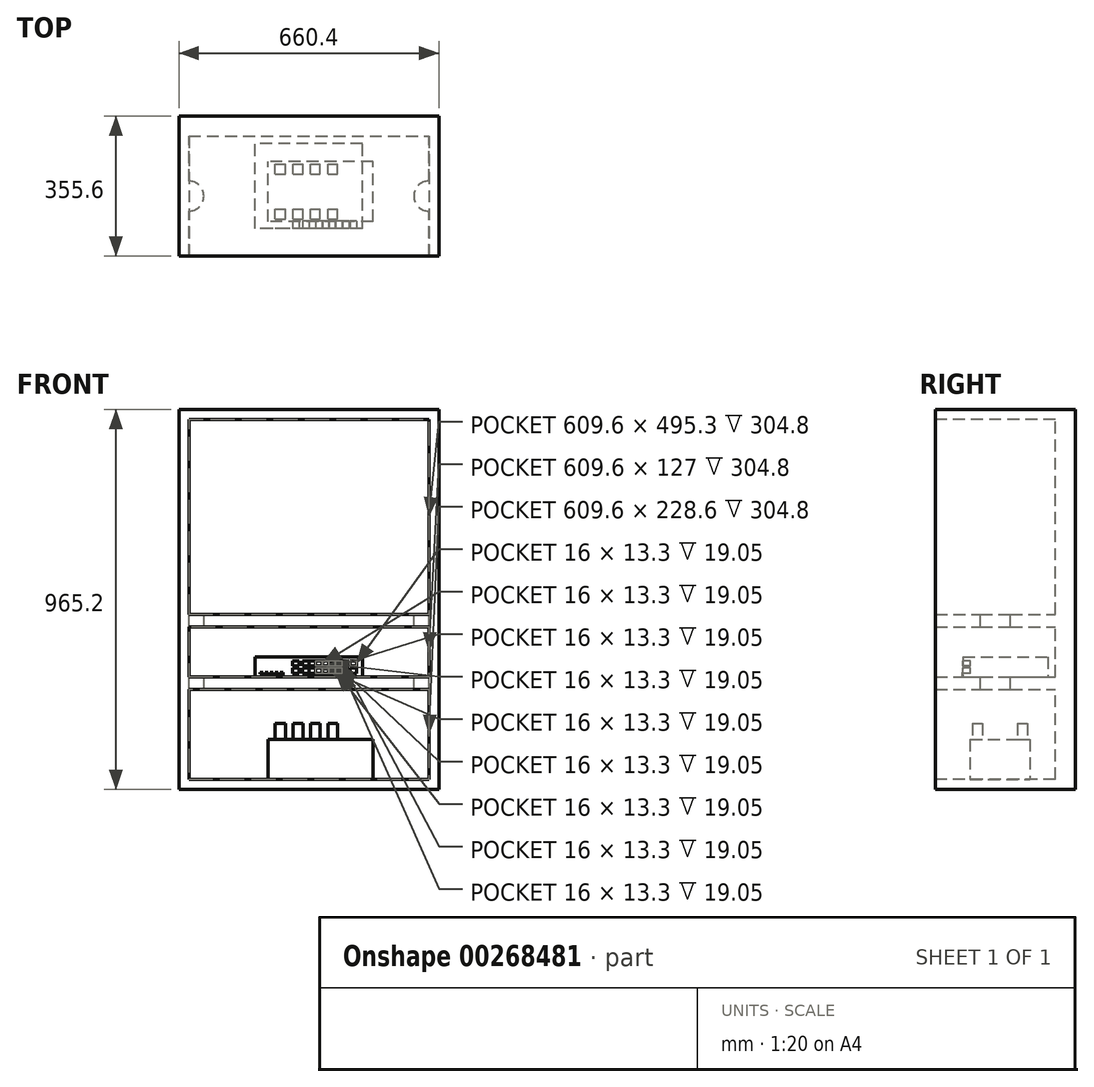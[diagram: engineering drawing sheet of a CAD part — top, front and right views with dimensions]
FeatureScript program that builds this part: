
annotation { "Feature Type Name" : "Feature", "Feature Type Description" : "" }
export const myFeature = defineFeature(function(context is Context, id is Id, definition is map)
    precondition{}
    {
        {
            var Q0;
            Q0=qCreatedBy(makeId("Top.planeOp"),FACE);
            var sketch = newSketch(context, id + "F0", { "sketchPlane" : qUnion([Q0])});
            skLineSegment(sketch, "E0.bottom", {"start": v(330.2, -177.8) * mm, "end": v(-330.2, -177.8) * mm});
            skLineSegment(sketch, "E0.top", {"start": v(330.2, 177.8) * mm, "end": v(-330.2, 177.8) * mm});
            skLineSegment(sketch, "E0.left", {"start": v(330.2, -177.8) * mm, "end": v(330.2, 177.8) * mm});
            skLineSegment(sketch, "E0.right", {"start": v(-330.2, -177.8) * mm, "end": v(-330.2, 177.8) * mm});
            skPoint(sketch, "E0.middle", {"position": v(0, 0) * mm});
            skSolve(sketch);
        }
        {
            var Q0;
            Q0 = qSketchRegion(id + "F0", true);
            extrude(context, id + "F1", {"entities" : qUnion([Q0]), "depth" : 965.2 * mm});
        }
        {
            var Q0;
            Q0=makeQuery(id+"F1.opExtrude","SWEPT_FACE",FACE,{"disambiguationData":[OSD([sQuery(id+"F0.wireOp",EDGE,"E0.bottom")])]});
            var sketch = newSketch(context, id + "F2", { "sketchPlane" : qUnion([Q0])});
            skLineSegment(sketch, "E1.bottom", {"start": v(304.8, 25.4) * mm, "end": v(-304.8, 25.4) * mm});
            skLineSegment(sketch, "E1.top", {"start": v(304.8, 939.8) * mm, "end": v(-304.8, 939.8) * mm});
            skLineSegment(sketch, "E1.left", {"start": v(304.8, 25.4) * mm, "end": v(304.8, 939.8) * mm});
            skLineSegment(sketch, "E1.right", {"start": v(-304.8, 25.4) * mm, "end": v(-304.8, 939.8) * mm});
            skPoint(sketch, "E1.middle", {"position": v(0, 482.6) * mm});
            skPoint(sketch, "E1.middle.positionSnap0", {"position": v(330.2, 482.6) * mm});
            skPoint(sketch, "E1.centerSnap0", {"position": v(330.2, 482.6) * mm});
            skSolve(sketch);
        }
        {
            var Q0;
            Q0 = qSketchRegion(id + "F2", true);
            extrude(context, id + "F3", {"entities" : qUnion([Q0]), "operationType" : NewBodyOperationType.REMOVE, "oppositeDirection" : true, "depth" : 304.8 * mm});
        }
        {
            var Q0;
            Q0=makeQuery(id+"F3.boolean.opBoolean","COPY",FACE,{"derivedFrom":makeQuery(id+"F3.opExtrude","CAP_FACE",FACE,{"disambiguationData":[OSD([sQuery(id+"F2.wireOp",EDGE,"E1.bottom"),sQuery(id+"F2.wireOp",EDGE,"E1.top"),sQuery(id+"F2.wireOp",EDGE,"E1.left"),sQuery(id+"F2.wireOp",EDGE,"E1.right")])],"isStart":false})});
            var sketch = newSketch(context, id + "F4", { "sketchPlane" : qUnion([Q0])});
            skLineSegment(sketch, "E2.bottom", {"start": v(-304.8, 254) * mm, "end": v(304.8, 254) * mm});
            skLineSegment(sketch, "E2.top", {"start": v(-304.8, 285.75) * mm, "end": v(304.8, 285.75) * mm});
            skLineSegment(sketch, "E2.left", {"start": v(-304.8, 254) * mm, "end": v(-304.8, 285.75) * mm});
            skLineSegment(sketch, "E2.right", {"start": v(304.8, 254) * mm, "end": v(304.8, 285.75) * mm});
            skLineSegment(sketch, "E3.bottom", {"start": v(-304.8, 412.75) * mm, "end": v(304.8, 412.75) * mm});
            skLineSegment(sketch, "E3.top", {"start": v(-304.8, 444.5) * mm, "end": v(304.8, 444.5) * mm});
            skLineSegment(sketch, "E3.left", {"start": v(-304.8, 412.75) * mm, "end": v(-304.8, 444.5) * mm});
            skLineSegment(sketch, "E3.right", {"start": v(304.8, 412.75) * mm, "end": v(304.8, 444.5) * mm});
            skSolve(sketch);
        }
        {
            var Q0;
            Q0 = qSketchRegion(id + "F4", true);
            extrude(context, id + "F5", {"entities" : qUnion([Q0]), "operationType" : NewBodyOperationType.ADD, "depth" : 304.8 * mm});
        }
        {
            var Q0;
            Q0=makeQuery(id+"F3.boolean.opBoolean","COPY",FACE,{"derivedFrom":makeQuery(id+"F3.opExtrude","SWEPT_FACE",FACE,{"disambiguationData":[OSD([sQuery(id+"F2.wireOp",EDGE,"E1.bottom")])]})});
            var sketch = newSketch(context, id + "F6", { "sketchPlane" : qUnion([Q0])});
            skLineSegment(sketch, "E4.bottom", {"start": v(162.51, -89.75) * mm, "end": v(-104.19, -89.75) * mm});
            skLineSegment(sketch, "E4.top", {"start": v(162.51, 62.65) * mm, "end": v(-104.19, 62.65) * mm});
            skLineSegment(sketch, "E4.left", {"start": v(162.51, -89.75) * mm, "end": v(162.51, 62.65) * mm});
            skLineSegment(sketch, "E4.right", {"start": v(-104.19, -89.75) * mm, "end": v(-104.19, 62.65) * mm});
            skPoint(sketch, "E4.middle", {"position": v(29.16, -13.55) * mm});
            skSolve(sketch);
        }
        {
            var Q0;
            Q0 = qSketchRegion(id + "F6", true);
            extrude(context, id + "F7", {"entities" : qUnion([Q0]), "operationType" : NewBodyOperationType.ADD, "depth" : 101.6 * mm});
        }
        {
            var Q0;
            Q0=makeQuery(id+"F7.opExtrude","CAP_FACE",FACE,{"disambiguationData":[OSD([sQuery(id+"F6.wireOp",EDGE,"E4.bottom"),sQuery(id+"F6.wireOp",EDGE,"E4.top"),sQuery(id+"F6.wireOp",EDGE,"E4.left"),sQuery(id+"F6.wireOp",EDGE,"E4.right")])],"isStart":false});
            var sketch = newSketch(context, id + "F8", { "sketchPlane" : qUnion([Q0])});
            skLineSegment(sketch, "E5.bottom", {"start": v(-85.14, -83.4) * mm, "end": v(-59.74, -83.4) * mm});
            skLineSegment(sketch, "E5.top", {"start": v(-85.14, -58) * mm, "end": v(-59.74, -58) * mm});
            skLineSegment(sketch, "E5.left", {"start": v(-85.14, -83.4) * mm, "end": v(-85.14, -58) * mm});
            skLineSegment(sketch, "E5.right", {"start": v(-59.74, -83.4) * mm, "end": v(-59.74, -58) * mm});
            skLineSegment(sketch, "E6.0.1.0", {"start": v(-85.14, 56.3) * mm, "end": v(-59.74, 56.3) * mm});
            skLineSegment(sketch, "E6.0.1.1", {"start": v(-85.14, 30.9) * mm, "end": v(-59.74, 30.9) * mm});
            skLineSegment(sketch, "E6.0.1.2", {"start": v(-59.74, 30.9) * mm, "end": v(-59.74, 56.3) * mm});
            skLineSegment(sketch, "E6.0.1.3", {"start": v(-85.14, 30.9) * mm, "end": v(-85.14, 56.3) * mm});
            skLineSegment(sketch, "E6.1.0.0", {"start": v(-40.69, -58) * mm, "end": v(-15.29, -58) * mm});
            skLineSegment(sketch, "E6.1.0.1", {"start": v(-40.69, -83.4) * mm, "end": v(-15.29, -83.4) * mm});
            skLineSegment(sketch, "E6.1.0.2", {"start": v(-15.29, -83.4) * mm, "end": v(-15.29, -58) * mm});
            skLineSegment(sketch, "E6.1.0.3", {"start": v(-40.69, -83.4) * mm, "end": v(-40.69, -58) * mm});
            skLineSegment(sketch, "E6.1.1.0", {"start": v(-40.69, 56.3) * mm, "end": v(-15.29, 56.3) * mm});
            skLineSegment(sketch, "E6.1.1.1", {"start": v(-40.69, 30.9) * mm, "end": v(-15.29, 30.9) * mm});
            skLineSegment(sketch, "E6.1.1.2", {"start": v(-15.29, 30.9) * mm, "end": v(-15.29, 56.3) * mm});
            skLineSegment(sketch, "E6.1.1.3", {"start": v(-40.69, 30.9) * mm, "end": v(-40.69, 56.3) * mm});
            skLineSegment(sketch, "E6.2.0.0", {"start": v(3.76, -58) * mm, "end": v(29.16, -58) * mm});
            skLineSegment(sketch, "E6.2.0.1", {"start": v(3.76, -83.4) * mm, "end": v(29.16, -83.4) * mm});
            skLineSegment(sketch, "E6.2.0.2", {"start": v(29.16, -83.4) * mm, "end": v(29.16, -58) * mm});
            skLineSegment(sketch, "E6.2.0.3", {"start": v(3.76, -83.4) * mm, "end": v(3.76, -58) * mm});
            skLineSegment(sketch, "E6.2.1.0", {"start": v(3.76, 56.3) * mm, "end": v(29.16, 56.3) * mm});
            skLineSegment(sketch, "E6.2.1.1", {"start": v(3.76, 30.9) * mm, "end": v(29.16, 30.9) * mm});
            skLineSegment(sketch, "E6.2.1.2", {"start": v(29.16, 30.9) * mm, "end": v(29.16, 56.3) * mm});
            skLineSegment(sketch, "E6.2.1.3", {"start": v(3.76, 30.9) * mm, "end": v(3.76, 56.3) * mm});
            skLineSegment(sketch, "E6.3.0.0", {"start": v(48.21, -58) * mm, "end": v(73.61, -58) * mm});
            skLineSegment(sketch, "E6.3.0.1", {"start": v(48.21, -83.4) * mm, "end": v(73.61, -83.4) * mm});
            skLineSegment(sketch, "E6.3.0.2", {"start": v(73.61, -83.4) * mm, "end": v(73.61, -58) * mm});
            skLineSegment(sketch, "E6.3.0.3", {"start": v(48.21, -83.4) * mm, "end": v(48.21, -58) * mm});
            skLineSegment(sketch, "E6.3.1.0", {"start": v(48.21, 56.3) * mm, "end": v(73.61, 56.3) * mm});
            skLineSegment(sketch, "E6.3.1.1", {"start": v(48.21, 30.9) * mm, "end": v(73.61, 30.9) * mm});
            skLineSegment(sketch, "E6.3.1.2", {"start": v(73.61, 30.9) * mm, "end": v(73.61, 56.3) * mm});
            skLineSegment(sketch, "E6.3.1.3", {"start": v(48.21, 30.9) * mm, "end": v(48.21, 56.3) * mm});
            skLineSegment(sketch, "E6.direction1", {"start": v(-85.14, -64.35) * mm, "end": v(-40.69, -64.35) * mm, "construction": true});
            skLineSegment(sketch, "E6.direction2", {"start": v(-85.14, -64.35) * mm, "end": v(-85.14, 49.95) * mm, "construction": true});
            skSolve(sketch);
        }
        {
            var Q0;
            Q0 = qSketchRegion(id + "F8", true);
            extrude(context, id + "F9", {"entities" : qUnion([Q0]), "operationType" : NewBodyOperationType.ADD, "depth" : 40.64 * mm});
        }
        {
            var Q0;
            Q0=makeQuery(id+"F5.opExtrude","SWEPT_FACE",FACE,{"disambiguationData":[OSD([sQuery(id+"F4.wireOp",EDGE,"E2.top")])]});
            var sketch = newSketch(context, id + "F10", { "sketchPlane" : qUnion([Q0])});
            skLineSegment(sketch, "E7.bottom", {"start": v(136.53, -107.95) * mm, "end": v(-136.53, -107.95) * mm});
            skLineSegment(sketch, "E7.top", {"start": v(136.53, 107.95) * mm, "end": v(-136.53, 107.95) * mm});
            skLineSegment(sketch, "E7.left", {"start": v(136.53, -107.95) * mm, "end": v(136.53, 107.95) * mm});
            skLineSegment(sketch, "E7.right", {"start": v(-136.53, -107.95) * mm, "end": v(-136.53, 107.95) * mm});
            skPoint(sketch, "E7.middle", {"position": v(0, 0) * mm});
            skSolve(sketch);
        }
        {
            var Q0;
            Q0=makeQuery(id+"F10.imprint","IMPRINT",FACE,{"disambiguationData":[TD([[makeQuery(id+"F10.imprint","IMPRINT",EDGE,{"derivedFrom":sQuery(id+"F10.wireOp",EDGE,"E7.bottom")}),-1.0]])]});
            extrude(context, id + "F11", {"entities" : qUnion([Q0]), "operationType" : NewBodyOperationType.ADD, "depth" : 50.8 * mm});
        }
        {
            var Q0;
            Q0=makeQuery(id+"F11.opExtrude","SWEPT_FACE",FACE,{"disambiguationData":[OSD([sQuery(id+"F10.wireOp",EDGE,"E7.bottom")])]});
            var sketch = newSketch(context, id + "F12", { "sketchPlane" : qUnion([Q0])});
            skLineSegment(sketch, "E8.bottom", {"start": v(0.12, 313.72) * mm, "end": v(-15.88, 313.72) * mm});
            skLineSegment(sketch, "E8.top", {"start": v(0.13, 327.02) * mm, "end": v(-15.88, 327.02) * mm});
            skLineSegment(sketch, "E8.left", {"start": v(0.13, 313.72) * mm, "end": v(0.12, 327.02) * mm});
            skLineSegment(sketch, "E8.right", {"start": v(-15.88, 313.72) * mm, "end": v(-15.88, 327.02) * mm});
            skPoint(sketch, "E8.middle", {"position": v(-7.88, 320.37) * mm});
            skPoint(sketch, "E9.0.1.0", {"position": v(-7.88, 301.93) * mm});
            skLineSegment(sketch, "E9.0.1.1", {"start": v(0.13, 295.28) * mm, "end": v(-15.88, 295.28) * mm});
            skLineSegment(sketch, "E9.0.1.2", {"start": v(0.13, 308.58) * mm, "end": v(-15.88, 308.58) * mm});
            skLineSegment(sketch, "E9.0.1.3", {"start": v(0.13, 295.28) * mm, "end": v(0.12, 308.58) * mm});
            skLineSegment(sketch, "E9.0.1.4", {"start": v(-15.87, 295.28) * mm, "end": v(-15.88, 308.58) * mm});
            skPoint(sketch, "E9.1.0.0", {"position": v(8.89, 320.37) * mm});
            skLineSegment(sketch, "E9.1.0.1", {"start": v(16.89, 313.72) * mm, "end": v(0.89, 313.72) * mm});
            skLineSegment(sketch, "E9.1.0.2", {"start": v(16.89, 327.02) * mm, "end": v(0.89, 327.02) * mm});
            skLineSegment(sketch, "E9.1.0.3", {"start": v(16.89, 313.72) * mm, "end": v(16.89, 327.02) * mm});
            skLineSegment(sketch, "E9.1.0.4", {"start": v(0.89, 313.72) * mm, "end": v(0.89, 327.02) * mm});
            skPoint(sketch, "E9.1.1.0", {"position": v(8.89, 301.93) * mm});
            skLineSegment(sketch, "E9.1.1.1", {"start": v(16.89, 295.28) * mm, "end": v(0.89, 295.28) * mm});
            skLineSegment(sketch, "E9.1.1.2", {"start": v(16.89, 308.58) * mm, "end": v(0.89, 308.58) * mm});
            skLineSegment(sketch, "E9.1.1.3", {"start": v(16.89, 295.28) * mm, "end": v(16.89, 308.58) * mm});
            skLineSegment(sketch, "E9.1.1.4", {"start": v(0.89, 295.28) * mm, "end": v(0.89, 308.58) * mm});
            skPoint(sketch, "E9.2.0.0", {"position": v(25.65, 320.37) * mm});
            skLineSegment(sketch, "E9.2.0.1", {"start": v(33.65, 313.72) * mm, "end": v(17.65, 313.72) * mm});
            skLineSegment(sketch, "E9.2.0.2", {"start": v(33.65, 327.02) * mm, "end": v(17.65, 327.02) * mm});
            skLineSegment(sketch, "E9.2.0.3", {"start": v(33.65, 313.72) * mm, "end": v(33.65, 327.02) * mm});
            skLineSegment(sketch, "E9.2.0.4", {"start": v(17.65, 313.72) * mm, "end": v(17.65, 327.02) * mm});
            skPoint(sketch, "E9.2.1.0", {"position": v(25.65, 301.93) * mm});
            skLineSegment(sketch, "E9.2.1.1", {"start": v(33.65, 295.28) * mm, "end": v(17.65, 295.28) * mm});
            skLineSegment(sketch, "E9.2.1.2", {"start": v(33.65, 308.58) * mm, "end": v(17.65, 308.58) * mm});
            skLineSegment(sketch, "E9.2.1.3", {"start": v(33.65, 295.28) * mm, "end": v(33.65, 308.58) * mm});
            skLineSegment(sketch, "E9.2.1.4", {"start": v(17.65, 295.28) * mm, "end": v(17.65, 308.58) * mm});
            skPoint(sketch, "E9.3.0.0", {"position": v(42.42, 320.37) * mm});
            skLineSegment(sketch, "E9.3.0.1", {"start": v(50.42, 313.72) * mm, "end": v(34.42, 313.72) * mm});
            skLineSegment(sketch, "E9.3.0.2", {"start": v(50.42, 327.02) * mm, "end": v(34.42, 327.02) * mm});
            skLineSegment(sketch, "E9.3.0.3", {"start": v(50.42, 313.72) * mm, "end": v(50.42, 327.02) * mm});
            skLineSegment(sketch, "E9.3.0.4", {"start": v(34.42, 313.72) * mm, "end": v(34.42, 327.02) * mm});
            skPoint(sketch, "E9.3.1.0", {"position": v(42.42, 301.93) * mm});
            skLineSegment(sketch, "E9.3.1.1", {"start": v(50.42, 295.28) * mm, "end": v(34.42, 295.28) * mm});
            skLineSegment(sketch, "E9.3.1.2", {"start": v(50.42, 308.58) * mm, "end": v(34.42, 308.58) * mm});
            skLineSegment(sketch, "E9.3.1.3", {"start": v(50.42, 295.28) * mm, "end": v(50.42, 308.58) * mm});
            skLineSegment(sketch, "E9.3.1.4", {"start": v(34.42, 295.28) * mm, "end": v(34.42, 308.58) * mm});
            skPoint(sketch, "E9.4.0.0", {"position": v(59.18, 320.37) * mm});
            skLineSegment(sketch, "E9.4.0.1", {"start": v(67.18, 313.72) * mm, "end": v(51.18, 313.72) * mm});
            skLineSegment(sketch, "E9.4.0.2", {"start": v(67.18, 327.02) * mm, "end": v(51.18, 327.02) * mm});
            skLineSegment(sketch, "E9.4.0.3", {"start": v(67.18, 313.72) * mm, "end": v(67.18, 327.02) * mm});
            skLineSegment(sketch, "E9.4.0.4", {"start": v(51.18, 313.72) * mm, "end": v(51.18, 327.02) * mm});
            skPoint(sketch, "E9.4.1.0", {"position": v(59.18, 301.93) * mm});
            skLineSegment(sketch, "E9.4.1.1", {"start": v(67.18, 295.28) * mm, "end": v(51.18, 295.28) * mm});
            skLineSegment(sketch, "E9.4.1.2", {"start": v(67.18, 308.58) * mm, "end": v(51.18, 308.58) * mm});
            skLineSegment(sketch, "E9.4.1.3", {"start": v(67.18, 295.28) * mm, "end": v(67.18, 308.58) * mm});
            skLineSegment(sketch, "E9.4.1.4", {"start": v(51.18, 295.28) * mm, "end": v(51.18, 308.58) * mm});
            skPoint(sketch, "E9.5.0.0", {"position": v(75.94, 320.37) * mm});
            skLineSegment(sketch, "E9.5.0.1", {"start": v(83.94, 313.72) * mm, "end": v(67.94, 313.72) * mm});
            skLineSegment(sketch, "E9.5.0.2", {"start": v(83.94, 327.02) * mm, "end": v(67.94, 327.02) * mm});
            skLineSegment(sketch, "E9.5.0.3", {"start": v(83.94, 313.72) * mm, "end": v(83.94, 327.02) * mm});
            skLineSegment(sketch, "E9.5.0.4", {"start": v(67.94, 313.72) * mm, "end": v(67.94, 327.02) * mm});
            skPoint(sketch, "E9.5.1.0", {"position": v(75.94, 301.93) * mm});
            skLineSegment(sketch, "E9.5.1.1", {"start": v(83.94, 295.28) * mm, "end": v(67.94, 295.28) * mm});
            skLineSegment(sketch, "E9.5.1.2", {"start": v(83.94, 308.58) * mm, "end": v(67.94, 308.58) * mm});
            skLineSegment(sketch, "E9.5.1.3", {"start": v(83.94, 295.28) * mm, "end": v(83.94, 308.58) * mm});
            skLineSegment(sketch, "E9.5.1.4", {"start": v(67.94, 295.28) * mm, "end": v(67.94, 308.58) * mm});
            skLineSegment(sketch, "E9.direction1", {"start": v(-15.88, 313.72) * mm, "end": v(0.89, 313.72) * mm, "construction": true});
            skLineSegment(sketch, "E9.direction2", {"start": v(-15.88, 313.72) * mm, "end": v(-15.88, 295.28) * mm, "construction": true});
            skLineSegment(sketch, "E10.1.0.0", {"start": v(-41.28, 313.72) * mm, "end": v(-25.27, 313.72) * mm, "construction": true});
            skLineSegment(sketch, "E10.1.0.1", {"start": v(-41.28, 313.72) * mm, "end": v(-41.28, 295.28) * mm, "construction": true});
            skPoint(sketch, "E10.1.0.2", {"position": v(-33.28, 301.93) * mm});
            skLineSegment(sketch, "E10.1.0.3", {"start": v(-25.28, 327.02) * mm, "end": v(-41.28, 327.02) * mm});
            skLineSegment(sketch, "E10.1.0.4", {"start": v(-41.28, 313.72) * mm, "end": v(-41.28, 327.02) * mm});
            skLineSegment(sketch, "E10.1.0.5", {"start": v(-25.28, 295.28) * mm, "end": v(-41.28, 295.28) * mm});
            skLineSegment(sketch, "E10.1.0.6", {"start": v(-25.28, 308.58) * mm, "end": v(-41.28, 308.58) * mm});
            skLineSegment(sketch, "E10.1.0.7", {"start": v(-25.28, 295.28) * mm, "end": v(-25.28, 308.58) * mm});
            skLineSegment(sketch, "E10.1.0.8", {"start": v(-25.27, 313.72) * mm, "end": v(-25.27, 327.02) * mm});
            skPoint(sketch, "E10.1.0.9", {"position": v(-33.28, 320.37) * mm});
            skLineSegment(sketch, "E10.1.0.10", {"start": v(-25.27, 295.28) * mm, "end": v(-25.27, 308.58) * mm});
            skLineSegment(sketch, "E10.1.0.11", {"start": v(-25.28, 313.72) * mm, "end": v(-41.28, 313.72) * mm});
            skLineSegment(sketch, "E10.1.0.12", {"start": v(-25.28, 313.72) * mm, "end": v(-25.28, 327.02) * mm});
            skLineSegment(sketch, "E10.1.0.13", {"start": v(-41.28, 295.28) * mm, "end": v(-41.28, 308.58) * mm});
            skLineSegment(sketch, "E11.1.0.0", {"start": v(85.72, 313.72) * mm, "end": v(101.73, 313.72) * mm, "construction": true});
            skLineSegment(sketch, "E11.1.0.1", {"start": v(101.72, 308.58) * mm, "end": v(85.72, 308.58) * mm});
            skLineSegment(sketch, "E11.1.0.2", {"start": v(101.73, 313.72) * mm, "end": v(101.73, 327.02) * mm});
            skLineSegment(sketch, "E11.1.0.3", {"start": v(85.72, 313.72) * mm, "end": v(85.72, 295.28) * mm, "construction": true});
            skPoint(sketch, "E11.1.0.4", {"position": v(93.73, 301.93) * mm});
            skLineSegment(sketch, "E11.1.0.5", {"start": v(101.73, 295.28) * mm, "end": v(101.73, 308.58) * mm});
            skLineSegment(sketch, "E11.1.0.6", {"start": v(101.72, 327.02) * mm, "end": v(85.72, 327.02) * mm});
            skPoint(sketch, "E11.1.0.7", {"position": v(93.73, 320.37) * mm});
            skLineSegment(sketch, "E11.1.0.8", {"start": v(101.72, 295.28) * mm, "end": v(85.72, 295.28) * mm});
            skLineSegment(sketch, "E11.1.0.9", {"start": v(85.72, 313.72) * mm, "end": v(85.72, 327.02) * mm});
            skLineSegment(sketch, "E11.1.0.10", {"start": v(101.72, 295.28) * mm, "end": v(101.72, 308.58) * mm});
            skLineSegment(sketch, "E11.1.0.11", {"start": v(85.72, 295.28) * mm, "end": v(85.72, 308.58) * mm});
            skLineSegment(sketch, "E11.1.0.12", {"start": v(101.72, 313.72) * mm, "end": v(101.72, 327.02) * mm});
            skLineSegment(sketch, "E11.1.0.13", {"start": v(101.72, 313.72) * mm, "end": v(85.72, 313.72) * mm});
            skLineSegment(sketch, "E12.1.0.0", {"start": v(120.77, 308.58) * mm, "end": v(104.77, 308.58) * mm});
            skLineSegment(sketch, "E12.1.0.1", {"start": v(120.77, 295.28) * mm, "end": v(104.77, 295.28) * mm});
            skPoint(sketch, "E12.1.0.2", {"position": v(112.78, 320.37) * mm});
            skLineSegment(sketch, "E12.1.0.3", {"start": v(120.77, 327.02) * mm, "end": v(104.77, 327.02) * mm});
            skLineSegment(sketch, "E12.1.0.4", {"start": v(120.78, 295.28) * mm, "end": v(120.78, 308.58) * mm});
            skPoint(sketch, "E12.1.0.5", {"position": v(112.78, 301.93) * mm});
            skLineSegment(sketch, "E12.1.0.6", {"start": v(120.77, 313.72) * mm, "end": v(120.77, 327.02) * mm});
            skLineSegment(sketch, "E12.1.0.7", {"start": v(104.77, 313.72) * mm, "end": v(104.77, 295.28) * mm, "construction": true});
            skLineSegment(sketch, "E12.1.0.8", {"start": v(104.77, 313.72) * mm, "end": v(120.78, 313.72) * mm, "construction": true});
            skLineSegment(sketch, "E12.1.0.9", {"start": v(104.77, 313.72) * mm, "end": v(104.77, 327.02) * mm});
            skLineSegment(sketch, "E12.1.0.10", {"start": v(120.77, 295.28) * mm, "end": v(120.77, 308.58) * mm});
            skLineSegment(sketch, "E12.1.0.11", {"start": v(120.77, 313.72) * mm, "end": v(104.77, 313.72) * mm});
            skLineSegment(sketch, "E12.1.0.12", {"start": v(104.77, 295.28) * mm, "end": v(104.77, 308.58) * mm});
            skLineSegment(sketch, "E12.1.0.13", {"start": v(120.78, 313.72) * mm, "end": v(120.78, 327.02) * mm});
            skLineSegment(sketch, "E12.direction1", {"start": v(85.72, 295.28) * mm, "end": v(104.77, 295.28) * mm, "construction": true});
            skLineSegment(sketch, "E13.bottom", {"start": v(-116.2, 294.02) * mm, "end": v(-123.83, 294.02) * mm});
            skLineSegment(sketch, "E13.top", {"start": v(-116.2, 297.83) * mm, "end": v(-123.83, 297.83) * mm});
            skLineSegment(sketch, "E13.left", {"start": v(-116.2, 294.02) * mm, "end": v(-116.2, 297.83) * mm});
            skLineSegment(sketch, "E13.right", {"start": v(-123.83, 294.02) * mm, "end": v(-123.83, 297.83) * mm});
            skPoint(sketch, "E13.middle", {"position": v(-120.02, 295.93) * mm});
            skLineSegment(sketch, "E14.1.0.0", {"start": v(-111.12, 294.02) * mm, "end": v(-111.12, 297.83) * mm});
            skLineSegment(sketch, "E14.1.0.1", {"start": v(-103.5, 294.02) * mm, "end": v(-111.12, 294.02) * mm});
            skLineSegment(sketch, "E14.1.0.2", {"start": v(-103.5, 294.02) * mm, "end": v(-103.5, 297.83) * mm});
            skPoint(sketch, "E14.1.0.3", {"position": v(-107.32, 295.93) * mm});
            skLineSegment(sketch, "E14.1.0.4", {"start": v(-103.5, 297.83) * mm, "end": v(-111.12, 297.83) * mm});
            skLineSegment(sketch, "E14.2.0.0", {"start": v(-98.42, 294.02) * mm, "end": v(-98.42, 297.83) * mm});
            skLineSegment(sketch, "E14.2.0.1", {"start": v(-90.8, 294.02) * mm, "end": v(-98.42, 294.02) * mm});
            skLineSegment(sketch, "E14.2.0.2", {"start": v(-90.8, 294.02) * mm, "end": v(-90.8, 297.83) * mm});
            skPoint(sketch, "E14.2.0.3", {"position": v(-94.62, 295.93) * mm});
            skLineSegment(sketch, "E14.2.0.4", {"start": v(-90.8, 297.83) * mm, "end": v(-98.42, 297.83) * mm});
            skLineSegment(sketch, "E14.3.0.0", {"start": v(-85.72, 294.02) * mm, "end": v(-85.72, 297.83) * mm});
            skLineSegment(sketch, "E14.3.0.1", {"start": v(-78.1, 294.02) * mm, "end": v(-85.72, 294.02) * mm});
            skLineSegment(sketch, "E14.3.0.2", {"start": v(-78.1, 294.02) * mm, "end": v(-78.1, 297.83) * mm});
            skPoint(sketch, "E14.3.0.3", {"position": v(-81.92, 295.93) * mm});
            skLineSegment(sketch, "E14.3.0.4", {"start": v(-78.1, 297.83) * mm, "end": v(-85.72, 297.83) * mm});
            skLineSegment(sketch, "E14.4.0.0", {"start": v(-73.02, 294.02) * mm, "end": v(-73.02, 297.83) * mm});
            skLineSegment(sketch, "E14.4.0.1", {"start": v(-65.4, 294.02) * mm, "end": v(-73.02, 294.02) * mm});
            skLineSegment(sketch, "E14.4.0.2", {"start": v(-65.4, 294.02) * mm, "end": v(-65.4, 297.83) * mm});
            skPoint(sketch, "E14.4.0.3", {"position": v(-69.22, 295.93) * mm});
            skLineSegment(sketch, "E14.4.0.4", {"start": v(-65.4, 297.83) * mm, "end": v(-73.02, 297.83) * mm});
            skLineSegment(sketch, "E14.direction1", {"start": v(-123.83, 294.02) * mm, "end": v(-111.12, 294.02) * mm, "construction": true});
            skPoint(sketch, "E15.0.1.0", {"position": v(-81.92, 290.34) * mm});
            skLineSegment(sketch, "E15.0.1.1", {"start": v(-85.72, 288.43) * mm, "end": v(-85.72, 292.24) * mm});
            skLineSegment(sketch, "E15.0.1.2", {"start": v(-78.1, 288.43) * mm, "end": v(-78.1, 292.24) * mm});
            skLineSegment(sketch, "E15.0.1.3", {"start": v(-103.5, 292.24) * mm, "end": v(-111.12, 292.24) * mm});
            skPoint(sketch, "E15.0.1.4", {"position": v(-94.62, 290.34) * mm});
            skLineSegment(sketch, "E15.0.1.5", {"start": v(-65.4, 288.43) * mm, "end": v(-65.4, 292.24) * mm});
            skLineSegment(sketch, "E15.0.1.6", {"start": v(-90.8, 292.24) * mm, "end": v(-98.42, 292.24) * mm});
            skLineSegment(sketch, "E15.0.1.7", {"start": v(-111.12, 288.43) * mm, "end": v(-111.12, 292.24) * mm});
            skLineSegment(sketch, "E15.0.1.8", {"start": v(-73.02, 288.43) * mm, "end": v(-73.02, 292.24) * mm});
            skLineSegment(sketch, "E15.0.1.9", {"start": v(-65.4, 292.24) * mm, "end": v(-73.02, 292.24) * mm});
            skLineSegment(sketch, "E15.0.1.10", {"start": v(-103.5, 288.43) * mm, "end": v(-103.5, 292.24) * mm});
            skPoint(sketch, "E15.0.1.11", {"position": v(-107.32, 290.34) * mm});
            skLineSegment(sketch, "E15.0.1.12", {"start": v(-78.1, 288.43) * mm, "end": v(-85.72, 288.43) * mm});
            skLineSegment(sketch, "E15.0.1.13", {"start": v(-90.8, 288.43) * mm, "end": v(-98.42, 288.43) * mm});
            skLineSegment(sketch, "E15.0.1.14", {"start": v(-78.1, 292.24) * mm, "end": v(-85.72, 292.24) * mm});
            skLineSegment(sketch, "E15.0.1.15", {"start": v(-98.42, 288.43) * mm, "end": v(-98.42, 292.24) * mm});
            skLineSegment(sketch, "E15.0.1.16", {"start": v(-65.4, 288.43) * mm, "end": v(-73.02, 288.43) * mm});
            skLineSegment(sketch, "E15.0.1.17", {"start": v(-90.8, 288.43) * mm, "end": v(-90.8, 292.24) * mm});
            skLineSegment(sketch, "E15.0.1.18", {"start": v(-103.5, 288.43) * mm, "end": v(-111.12, 288.43) * mm});
            skPoint(sketch, "E15.0.1.19", {"position": v(-69.22, 290.34) * mm});
            skLineSegment(sketch, "E15.direction1", {"start": v(-111.12, 294.02) * mm, "end": v(-85.72, 294.02) * mm, "construction": true});
            skLineSegment(sketch, "E15.direction2", {"start": v(-111.12, 294.02) * mm, "end": v(-111.12, 288.43) * mm, "construction": true});
            skSolve(sketch);
        }
        {
            var Q0;
            Q0=makeQuery(id+"F12.imprint","IMPRINT",FACE,{"disambiguationData":[TD([[makeQuery(id+"F12.imprint","IMPRINT",EDGE,{"derivedFrom":sQuery(id+"F12.wireOp",EDGE,"E12.1.0.0")}),1.0]])]});
            var Q1;
            Q1=makeQuery(id+"F12.imprint","IMPRINT",FACE,{"disambiguationData":[TD([[makeQuery(id+"F12.imprint","IMPRINT",EDGE,{"derivedFrom":sQuery(id+"F12.wireOp",EDGE,"E12.1.0.3")}),1.0]])]});
            var Q2;
            Q2=makeQuery(id+"F12.imprint","IMPRINT",FACE,{"disambiguationData":[TD([[makeQuery(id+"F12.imprint","IMPRINT",EDGE,{"derivedFrom":sQuery(id+"F12.wireOp",EDGE,"E11.1.0.6")}),1.0]])]});
            var Q3;
            Q3=makeQuery(id+"F12.imprint","IMPRINT",FACE,{"disambiguationData":[TD([[makeQuery(id+"F12.imprint","IMPRINT",EDGE,{"derivedFrom":sQuery(id+"F12.wireOp",EDGE,"E10.1.0.5")}),-1.0]])]});
            var Q4;
            Q4=makeQuery(id+"F12.imprint","IMPRINT",FACE,{"disambiguationData":[TD([[makeQuery(id+"F12.imprint","IMPRINT",EDGE,{"derivedFrom":sQuery(id+"F12.wireOp",EDGE,"E11.1.0.1")}),1.0]])]});
            var Q5;
            Q5=makeQuery(id+"F12.imprint","IMPRINT",FACE,{"disambiguationData":[TD([[makeQuery(id+"F12.imprint","IMPRINT",EDGE,{"derivedFrom":sQuery(id+"F12.wireOp",EDGE,"E8.bottom")}),-1.0]])]});
            var Q6;
            Q6=makeQuery(id+"F12.imprint","IMPRINT",FACE,{"disambiguationData":[TD([[makeQuery(id+"F12.imprint","IMPRINT",EDGE,{"derivedFrom":sQuery(id+"F12.wireOp",EDGE,"E9.0.1.1")}),-1.0]])]});
            var Q7;
            Q7=makeQuery(id+"F12.imprint","IMPRINT",FACE,{"disambiguationData":[TD([[makeQuery(id+"F12.imprint","IMPRINT",EDGE,{"derivedFrom":sQuery(id+"F12.wireOp",EDGE,"E9.1.0.1")}),-1.0]])]});
            var Q8;
            Q8=makeQuery(id+"F12.imprint","IMPRINT",FACE,{"disambiguationData":[TD([[makeQuery(id+"F12.imprint","IMPRINT",EDGE,{"derivedFrom":sQuery(id+"F12.wireOp",EDGE,"E9.1.1.1")}),-1.0]])]});
            var Q9;
            Q9=makeQuery(id+"F12.imprint","IMPRINT",FACE,{"disambiguationData":[TD([[makeQuery(id+"F12.imprint","IMPRINT",EDGE,{"derivedFrom":sQuery(id+"F12.wireOp",EDGE,"E9.2.0.1")}),-1.0]])]});
            var Q10;
            Q10=makeQuery(id+"F12.imprint","IMPRINT",FACE,{"disambiguationData":[TD([[makeQuery(id+"F12.imprint","IMPRINT",EDGE,{"derivedFrom":sQuery(id+"F12.wireOp",EDGE,"E9.2.1.1")}),-1.0]])]});
            var Q11;
            Q11=makeQuery(id+"F12.imprint","IMPRINT",FACE,{"disambiguationData":[TD([[makeQuery(id+"F12.imprint","IMPRINT",EDGE,{"derivedFrom":sQuery(id+"F12.wireOp",EDGE,"E9.3.0.1")}),-1.0]])]});
            var Q12;
            Q12=makeQuery(id+"F12.imprint","IMPRINT",FACE,{"disambiguationData":[TD([[makeQuery(id+"F12.imprint","IMPRINT",EDGE,{"derivedFrom":sQuery(id+"F12.wireOp",EDGE,"E9.3.1.1")}),-1.0]])]});
            var Q13;
            Q13=makeQuery(id+"F12.imprint","IMPRINT",FACE,{"disambiguationData":[TD([[makeQuery(id+"F12.imprint","IMPRINT",EDGE,{"derivedFrom":sQuery(id+"F12.wireOp",EDGE,"E9.4.0.1")}),-1.0]])]});
            var Q14;
            Q14=makeQuery(id+"F12.imprint","IMPRINT",FACE,{"disambiguationData":[TD([[makeQuery(id+"F12.imprint","IMPRINT",EDGE,{"derivedFrom":sQuery(id+"F12.wireOp",EDGE,"E9.4.1.1")}),-1.0]])]});
            var Q15;
            Q15=makeQuery(id+"F12.imprint","IMPRINT",FACE,{"disambiguationData":[TD([[makeQuery(id+"F12.imprint","IMPRINT",EDGE,{"derivedFrom":sQuery(id+"F12.wireOp",EDGE,"E9.5.0.1")}),-1.0]])]});
            var Q16;
            Q16=makeQuery(id+"F12.imprint","IMPRINT",FACE,{"disambiguationData":[TD([[makeQuery(id+"F12.imprint","IMPRINT",EDGE,{"derivedFrom":sQuery(id+"F12.wireOp",EDGE,"E9.5.1.1")}),-1.0]])]});
            var Q17;
            Q17=makeQuery(id+"F12.imprint","IMPRINT",FACE,{"disambiguationData":[TD([[makeQuery(id+"F12.imprint","IMPRINT",EDGE,{"derivedFrom":sQuery(id+"F12.wireOp",EDGE,"E10.1.0.3")}),1.0]])]});
            extrude(context, id + "F13", {"entities" : qUnion([Q0, Q1, Q2, Q3, Q4, Q5, Q6, Q7, Q8, Q9, Q10, Q11, Q12, Q13, Q14, Q15, Q16, Q17]), "operationType" : NewBodyOperationType.REMOVE, "oppositeDirection" : true, "depth" : 19.05 * mm});
        }
        {
            var Q0;
            Q0=makeQuery(id+"F12.imprint","IMPRINT",FACE,{"disambiguationData":[TD([[makeQuery(id+"F12.imprint","IMPRINT",EDGE,{"derivedFrom":sQuery(id+"F12.wireOp",EDGE,"E13.bottom")}),-1.0]])]});
            var Q1;
            Q1=makeQuery(id+"F12.imprint","IMPRINT",FACE,{"disambiguationData":[TD([[makeQuery(id+"F12.imprint","IMPRINT",EDGE,{"derivedFrom":sQuery(id+"F12.wireOp",EDGE,"E14.1.0.0")}),-1.0]])]});
            var Q2;
            Q2=makeQuery(id+"F12.imprint","IMPRINT",FACE,{"disambiguationData":[TD([[makeQuery(id+"F12.imprint","IMPRINT",EDGE,{"derivedFrom":sQuery(id+"F12.wireOp",EDGE,"E14.2.0.0")}),-1.0]])]});
            var Q3;
            Q3=makeQuery(id+"F12.imprint","IMPRINT",FACE,{"disambiguationData":[TD([[makeQuery(id+"F12.imprint","IMPRINT",EDGE,{"derivedFrom":sQuery(id+"F12.wireOp",EDGE,"E14.3.0.0")}),-1.0]])]});
            var Q4;
            Q4=makeQuery(id+"F12.imprint","IMPRINT",FACE,{"disambiguationData":[TD([[makeQuery(id+"F12.imprint","IMPRINT",EDGE,{"derivedFrom":sQuery(id+"F12.wireOp",EDGE,"E14.4.0.0")}),-1.0]])]});
            var Q5;
            Q5=makeQuery(id+"F12.imprint","IMPRINT",FACE,{"disambiguationData":[TD([[makeQuery(id+"F12.imprint","IMPRINT",EDGE,{"derivedFrom":sQuery(id+"F12.wireOp",EDGE,"E15.0.1.1")}),-1.0]])]});
            var Q6;
            Q6=makeQuery(id+"F12.imprint","IMPRINT",FACE,{"disambiguationData":[TD([[makeQuery(id+"F12.imprint","IMPRINT",EDGE,{"derivedFrom":sQuery(id+"F12.wireOp",EDGE,"E15.0.1.3")}),1.0]])]});
            var Q7;
            Q7=makeQuery(id+"F12.imprint","IMPRINT",FACE,{"disambiguationData":[TD([[makeQuery(id+"F12.imprint","IMPRINT",EDGE,{"derivedFrom":sQuery(id+"F12.wireOp",EDGE,"E15.0.1.5")}),1.0]])]});
            var Q8;
            Q8=makeQuery(id+"F12.imprint","IMPRINT",FACE,{"disambiguationData":[TD([[makeQuery(id+"F12.imprint","IMPRINT",EDGE,{"derivedFrom":sQuery(id+"F12.wireOp",EDGE,"E15.0.1.6")}),1.0]])]});
            var Q9;
            Q9 = qSketchRegion(id + "Fo3EQjvO2vu90ts_1", true);
            extrude(context, id + "F14", {"entities" : qUnion([Q0, Q1, Q2, Q3, Q4, Q5, Q6, Q7, Q8, Q9]), "operationType" : NewBodyOperationType.ADD, "oppositeDirection" : true, "depth" : 1.27 * mm, "symmetric" : true});
        }
        {
            var Q0;
            Q0=makeQuery(id+"F5.opExtrude","SWEPT_FACE",FACE,{"disambiguationData":[OSD([sQuery(id+"F4.wireOp",EDGE,"E3.top")])]});
            var sketch = newSketch(context, id + "F15", { "sketchPlane" : qUnion([Q0])});
            skArc(sketch, "E16", {"start": v(304.8, 12.7) * mm, "mid": v(266.7, -25.4) * mm, "end": v(304.8, -63.5) * mm});
            skArc(sketch, "E17", {"start": v(-304.8, -63.5) * mm, "mid": v(-266.7, -25.4) * mm, "end": v(-304.8, 12.7) * mm});
            skSolve(sketch);
        }
        {
            var Q0;
            {var subQ0=sQuery(id+"F15.wireOp",EDGE,"E17");Q0=makeQuery(id+"F15.imprint","IMPRINT",FACE,{"disambiguationData":[TD([[makeQuery(id+"F15.imprint","IMPRINT",EDGE,{"derivedFrom":subQ0}),1.0]])]});}
            var Q1;
            {var subQ0=sQuery(id+"F15.wireOp",EDGE,"E16");Q1=makeQuery(id+"F15.imprint","IMPRINT",FACE,{"disambiguationData":[TD([[makeQuery(id+"F15.imprint","IMPRINT",EDGE,{"derivedFrom":subQ0}),1.0]])]});}
            extrude(context, id + "F16", {"entities" : qUnion([Q0, Q1]), "operationType" : NewBodyOperationType.REMOVE, "oppositeDirection" : true, "depth" : 190.5 * mm});
        }
    });
